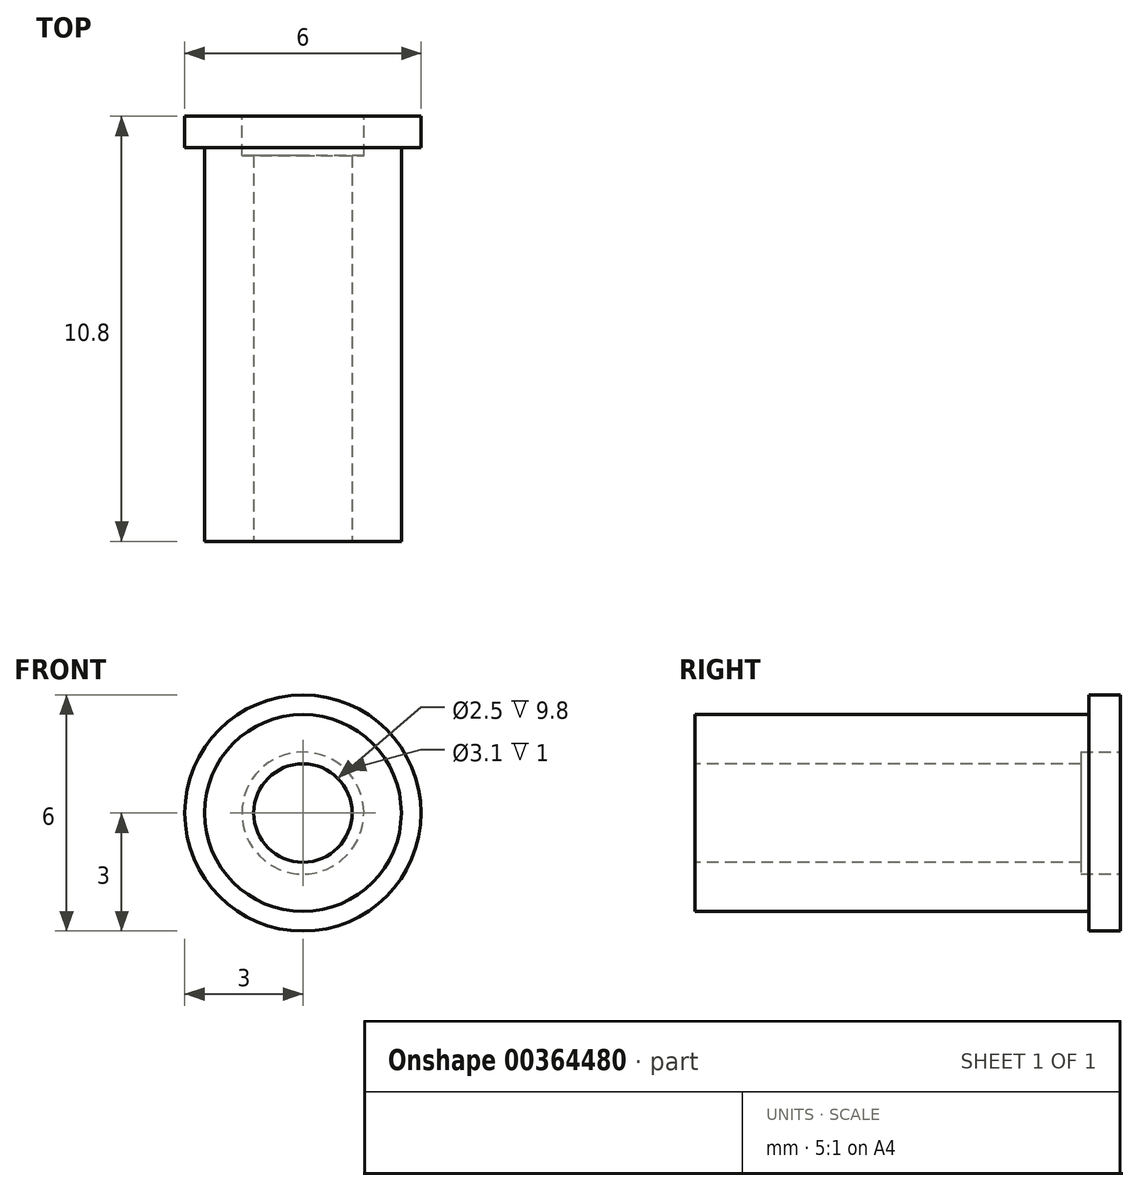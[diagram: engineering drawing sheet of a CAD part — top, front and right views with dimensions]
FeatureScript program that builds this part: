
annotation { "Feature Type Name" : "Feature", "Feature Type Description" : "" }
export const myFeature = defineFeature(function(context is Context, id is Id, definition is map)
    precondition{}
    {
        {
            var Q0;
            Q0=qCreatedBy(makeId("Front.planeOp"),FACE);
            var sketch = newSketch(context, id + "F0", { "sketchPlane" : qUnion([Q0])});
            skCircle(sketch, "E0", {"center": v(0, 0) * mm, "radius": 3 * mm});
            skSolve(sketch);
        }
        {
            var Q0;
            Q0=makeQuery(id+"F0.imprint","IMPRINT",FACE,{"disambiguationData":[TD([[makeQuery(id+"F0.imprint","IMPRINT",EDGE,{"derivedFrom":sQuery(id+"F0.wireOp",EDGE,"E0")}),1.0]])]});
            extrude(context, id + "F1", {"entities" : qUnion([Q0]), "depth" : 0.8 * mm});
        }
        {
            var Q0;
            Q0=makeQuery(id+"F1.opExtrude","CAP_FACE",FACE,{"disambiguationData":[OSD([sQuery(id+"F0.wireOp",EDGE,"E0")])],"isStart":false});
            var sketch = newSketch(context, id + "F2", { "sketchPlane" : qUnion([Q0])});
            skCircle(sketch, "E1", {"center": v(0, 0) * mm, "radius": 2.5 * mm});
            skSolve(sketch);
        }
        {
            var Q0;
            Q0 = qSketchRegion(id + "F2", true);
            extrude(context, id + "F3", {"entities" : qUnion([Q0]), "operationType" : NewBodyOperationType.ADD, "depth" : 10 * mm});
        }
        {
            var Q0;
            Q0=makeQuery(id+"F3.opExtrude","CAP_FACE",FACE,{"disambiguationData":[OSD([sQuery(id+"F2.wireOp",EDGE,"E1")])],"isStart":false});
            var sketch = newSketch(context, id + "F4", { "sketchPlane" : qUnion([Q0])});
            skCircle(sketch, "E2", {"center": v(0, 0) * mm, "radius": 1.25 * mm});
            skSolve(sketch);
        }
        {
            var Q0;
            Q0 = qSketchRegion(id + "F4", true);
            extrude(context, id + "F5", {"entities" : qUnion([Q0]), "operationType" : NewBodyOperationType.REMOVE, "oppositeDirection" : true, "depth" : 25 * mm});
        }
        {
            var Q0;
            Q0=makeQuery(id+"F1.opExtrude","CAP_FACE",FACE,{"disambiguationData":[OSD([sQuery(id+"F0.wireOp",EDGE,"E0")])],"isStart":true});
            var sketch = newSketch(context, id + "F6", { "sketchPlane" : qUnion([Q0])});
            skCircle(sketch, "E3", {"center": v(0, 0) * mm, "radius": 1.55 * mm});
            skSolve(sketch);
        }
        {
            var Q0;
            Q0 = qSketchRegion(id + "F6", true);
            var Q1;
            Q1=makeQuery(id+"F6.imprint","IMPRINT",FACE,{"disambiguationData":[TD([[makeQuery(id+"F6.imprint","IMPRINT",EDGE,{"derivedFrom":makeQuery(id+"F5.boolean.opBoolean","INTERSECT",EDGE,{"derivedFrom":[makeQuery(id+"F1.opExtrude","CAP_FACE",FACE,{"disambiguationData":[OSD([sQuery(id+"F0.wireOp",EDGE,"E0")])],"isStart":true}),makeQuery(id+"F5.opExtrude","SWEPT_FACE",FACE,{"disambiguationData":[OSD([sQuery(id+"F4.wireOp",EDGE,"E2")])]})]})}),-1.0]])]});
            extrude(context, id + "F7", {"entities" : qUnion([Q0, Q1]), "operationType" : NewBodyOperationType.REMOVE, "oppositeDirection" : true, "depth" : 1 * mm});
        }
    });
